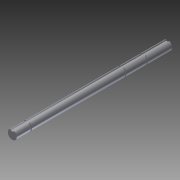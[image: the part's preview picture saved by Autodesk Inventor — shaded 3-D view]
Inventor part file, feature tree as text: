
AUTODESK INVENTOR PART (.ipt)
format: ipt  version: 2012 (Build 160160000, 160)  size: 108,032 bytes
history: native  units: in
note: dims shown in document units (in); Inventor stores cm internally (conversion verified against a paired STEP export)
features: extrude x5, plane x5, sketch x4, projected_geometry x1
ambient origin geometry x8: Origin, YZ Plane, XZ Plane, XY Plane, X Axis, Y Axis, Z Axis, Center Point
bodies: Solid1 (feature_tree)
feature tree (15):
  sketch  "Sketch1"  dims[d0=0.375in d1=6.498in d2=0.0in]
  extrude  "Extrusion1"  Depth=6.498in TaperAngle=0.0deg
  plane  "Work Plane6"
  plane  "Work Plane12"
  extrude  "Extrusion11"  Depth=0.045in TaperAngle=0.0deg
  plane  "Work Plane13"
  extrude  "Extrusion12"  Depth=0.045in TaperAngle=0.0deg
  plane  "Work Plane14"
  extrude  "Extrusion13"  Depth=0.045in TaperAngle=0.0deg
  plane  "Work Plane15"
  extrude  "Extrusion14"  [1 undecoded]
  sketch  "Sketch10"  dims[d33=-0.634in d34=0.045in d35=0.0in]
  sketch  "Sketch11"  dims[d36=-1.959in d37=0.045in d38=0.0in]
  projected_geometry  "Projected Loop2"
  sketch  "Sketch12"  dims[d39=-1.055in d40=0.045in d41=0.0in d42=-0.635in d43=0.125in d44=0.125in d45=0.0625in d46=0.25in d47=0.045in d48=0.0in]
note: 1 required parameter value undecoded (feature->parameter linkage not recoverable at this tier; creation-order binding heuristic only, values carry confidence <= 0.55)
